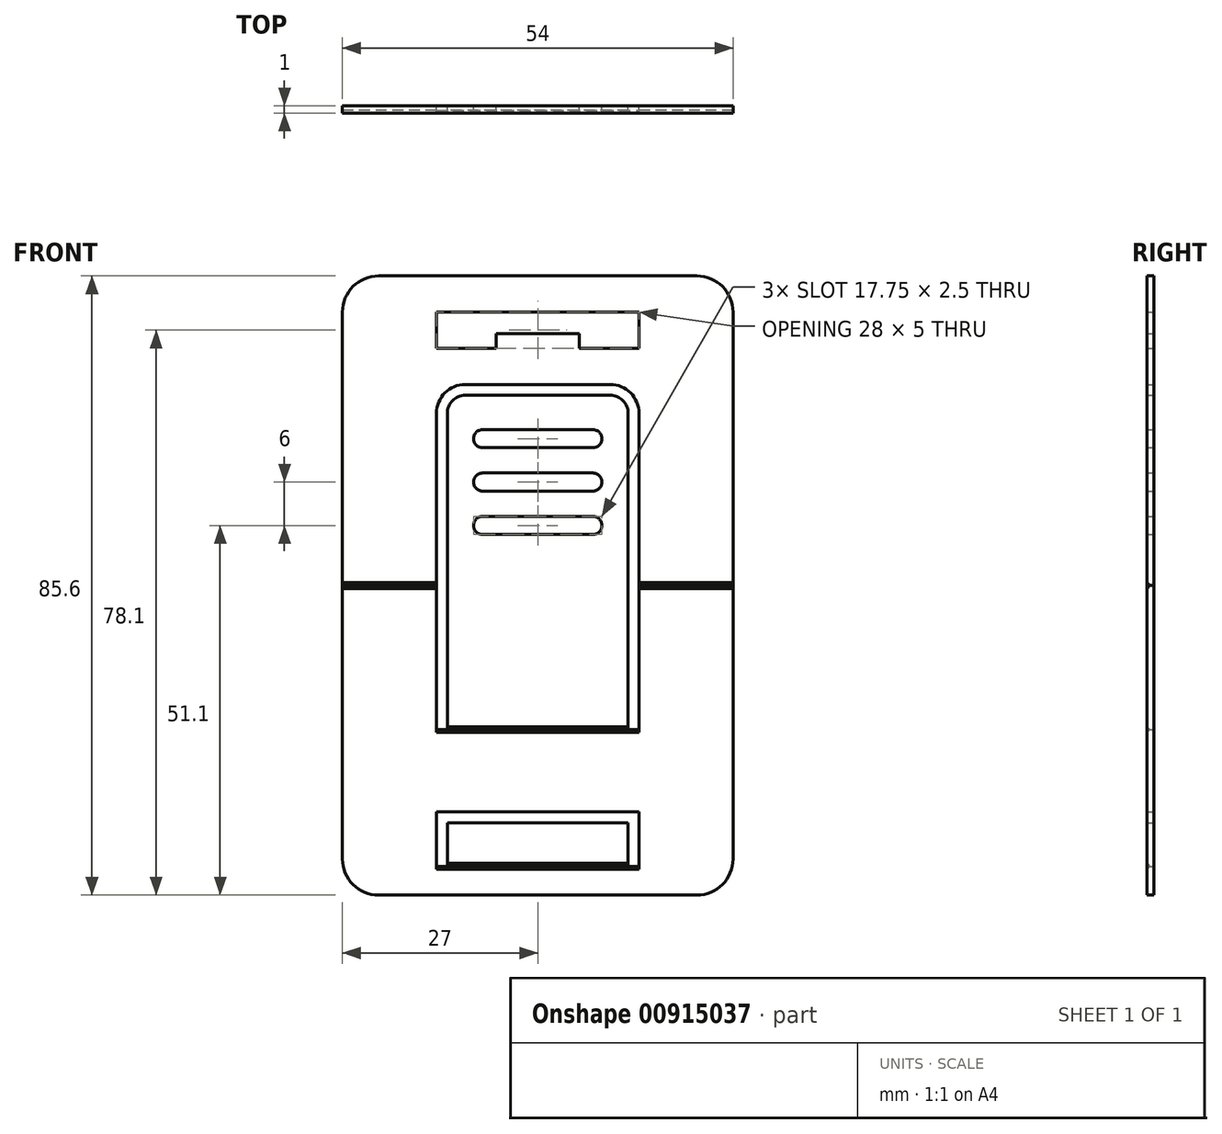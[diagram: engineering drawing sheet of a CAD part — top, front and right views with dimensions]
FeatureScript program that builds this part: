
annotation { "Feature Type Name" : "Feature", "Feature Type Description" : "" }
export const myFeature = defineFeature(function(context is Context, id is Id, definition is map)
    precondition{}
    {
        {
            var Q0;
            Q0=qCreatedBy(makeId("Front.planeOp"),FACE);
            var sketch = newSketch(context, id + "F0", { "sketchPlane" : qUnion([Q0])});
            skLineSegment(sketch, "E0.bottom", {"start": v(-22, 85.6) * mm, "end": v(22, 85.6) * mm});
            skLineSegment(sketch, "E0.top", {"start": v(-22, 0) * mm, "end": v(22, 0) * mm});
            skLineSegment(sketch, "E0.left", {"start": v(-27, 80.6) * mm, "end": v(-27, 5) * mm});
            skLineSegment(sketch, "E0.right", {"start": v(27, 80.6) * mm, "end": v(27, 5) * mm});
            skPoint(sketch, "E1.visualSharp", {"position": v(-27, 85.6) * mm});
            skArc(sketch, "E1.filletArc", {"start": v(-22, 85.6) * mm, "mid": v(-25.54, 84.14) * mm, "end": v(-27, 80.6) * mm});
            skPoint(sketch, "E2.visualSharp", {"position": v(-27, 0) * mm});
            skArc(sketch, "E2.filletArc", {"start": v(-27, 5) * mm, "mid": v(-25.54, 1.46) * mm, "end": v(-22, 0) * mm});
            skPoint(sketch, "E3.visualSharp", {"position": v(27, 0) * mm});
            skArc(sketch, "E3.filletArc", {"start": v(22, 0) * mm, "mid": v(25.54, 1.46) * mm, "end": v(27, 5) * mm});
            skPoint(sketch, "E4.visualSharp", {"position": v(27, 85.6) * mm});
            skArc(sketch, "E4.filletArc", {"start": v(27, 80.6) * mm, "mid": v(25.54, 84.14) * mm, "end": v(22, 85.6) * mm});
            skLineSegment(sketch, "E5.bottom", {"start": v(-10, 70.6) * mm, "end": v(10, 70.6) * mm});
            skLineSegment(sketch, "E5.left", {"start": v(-14, 66.6) * mm, "end": v(-14, 22.88) * mm});
            skLineSegment(sketch, "E5.right", {"start": v(14, 66.6) * mm, "end": v(14, 22.88) * mm});
            skPoint(sketch, "E6.visualSharp", {"position": v(-14, 70.6) * mm});
            skArc(sketch, "E6.filletArc", {"start": v(-10, 70.6) * mm, "mid": v(-12.83, 69.43) * mm, "end": v(-14, 66.6) * mm});
            skPoint(sketch, "E7.visualSharp", {"position": v(14, 70.6) * mm});
            skArc(sketch, "E7.filletArc", {"start": v(14, 66.6) * mm, "mid": v(12.83, 69.43) * mm, "end": v(10, 70.6) * mm});
            skPoint(sketch, "E8", {"position": v(0, 70.6) * mm});
            skPoint(sketch, "E9", {"position": v(0, 85.6) * mm});
            skLineSegment(sketch, "E10.0", {"start": v(-12.5, 66.6) * mm, "end": v(-12.5, 22.88) * mm});
            skLineSegment(sketch, "E10.1", {"start": v(12.5, 66.6) * mm, "end": v(12.5, 22.88) * mm});
            skArc(sketch, "E10.2", {"start": v(12.5, 66.6) * mm, "mid": v(11.77, 68.37) * mm, "end": v(10, 69.1) * mm});
            skLineSegment(sketch, "E10.3", {"start": v(-10, 69.1) * mm, "end": v(10, 69.1) * mm});
            skArc(sketch, "E10.4", {"start": v(-10, 69.1) * mm, "mid": v(-11.77, 68.37) * mm, "end": v(-12.5, 66.6) * mm});
            skLineSegment(sketch, "E11", {"start": v(-12.5, 22.88) * mm, "end": v(-14, 22.88) * mm});
            skLineSegment(sketch, "E12", {"start": v(12.5, 22.88) * mm, "end": v(14, 22.88) * mm});
            skLineSegment(sketch, "E13", {"start": v(-12.5, 22.88) * mm, "end": v(12.5, 22.88) * mm});
            skLineSegment(sketch, "E14.bottom", {"start": v(-14, 80.6) * mm, "end": v(14, 80.6) * mm});
            skLineSegment(sketch, "E14.top", {"start": v(-14, 75.6) * mm, "end": v(-5.74, 75.6) * mm});
            skLineSegment(sketch, "E14.left", {"start": v(-14, 80.6) * mm, "end": v(-14, 75.6) * mm});
            skLineSegment(sketch, "E14.right", {"start": v(14, 80.6) * mm, "end": v(14, 75.6) * mm});
            skPoint(sketch, "E15", {"position": v(0, 75.6) * mm});
            skLineSegment(sketch, "E16", {"start": v(-5.74, 75.6) * mm, "end": v(-5.74, 77.6) * mm});
            skLineSegment(sketch, "E17", {"start": v(-5.74, 77.6) * mm, "end": v(5.74, 77.6) * mm});
            skLineSegment(sketch, "E18", {"start": v(5.74, 77.6) * mm, "end": v(5.74, 75.6) * mm});
            skPoint(sketch, "E19", {"position": v(0, 77.6) * mm});
            skLineSegment(sketch, "E20.trimOffspring", {"start": v(5.74, 75.6) * mm, "end": v(14, 75.6) * mm});
            skLineSegment(sketch, "E21", {"start": v(-27, 42.8) * mm, "end": v(-14, 42.8) * mm});
            skLineSegment(sketch, "E22", {"start": v(27, 42.8) * mm, "end": v(14, 42.8) * mm});
            skLineSegment(sketch, "E23.top", {"start": v(-14, 11.5) * mm, "end": v(14, 11.5) * mm});
            skLineSegment(sketch, "E23.left", {"start": v(-14, 4) * mm, "end": v(-14, 11.5) * mm});
            skLineSegment(sketch, "E23.right", {"start": v(14, 4) * mm, "end": v(14, 11.5) * mm});
            skPoint(sketch, "E24", {"position": v(0, 11.5) * mm});
            skLineSegment(sketch, "E25.0", {"start": v(12.5, 4) * mm, "end": v(12.5, 10) * mm});
            skLineSegment(sketch, "E25.1", {"start": v(-12.5, 10) * mm, "end": v(12.5, 10) * mm});
            skLineSegment(sketch, "E25.2", {"start": v(-12.5, 4) * mm, "end": v(-12.5, 10) * mm});
            skLineSegment(sketch, "E26", {"start": v(-14, 4) * mm, "end": v(-12.5, 4) * mm});
            skLineSegment(sketch, "E27", {"start": v(12.5, 4) * mm, "end": v(14, 4) * mm});
            skLineSegment(sketch, "E28", {"start": v(-12.5, 4) * mm, "end": v(12.5, 4) * mm});
            skLineSegment(sketch, "E29", {"start": v(-7.62, 63.1) * mm, "end": v(7.62, 63.1) * mm, "construction": true});
            skLineSegment(sketch, "E30", {"start": v(-7.62, 57.1) * mm, "end": v(7.62, 57.1) * mm, "construction": true});
            skLineSegment(sketch, "E31", {"start": v(-7.62, 51.1) * mm, "end": v(7.62, 51.1) * mm, "construction": true});
            skLineSegment(sketch, "E32", {"start": v(0, 63.1) * mm, "end": v(0, 57.1) * mm, "construction": true});
            skLineSegment(sketch, "E33", {"start": v(0, 51.1) * mm, "end": v(0, 57.1) * mm, "construction": true});
            skArc(sketch, "E34.0.startCap", {"start": v(-7.62, 61.85) * mm, "mid": v(-8.87, 63.1) * mm, "end": v(-7.62, 64.35) * mm});
            skArc(sketch, "E34.0.endCap", {"start": v(7.62, 64.35) * mm, "mid": v(8.87, 63.1) * mm, "end": v(7.62, 61.85) * mm});
            skLineSegment(sketch, "E34.0.left", {"start": v(-7.62, 64.35) * mm, "end": v(7.62, 64.35) * mm});
            skLineSegment(sketch, "E34.0.right", {"start": v(-7.62, 61.85) * mm, "end": v(7.62, 61.85) * mm});
            skArc(sketch, "E34.1.startCap", {"start": v(-7.62, 55.85) * mm, "mid": v(-8.87, 57.1) * mm, "end": v(-7.62, 58.35) * mm});
            skArc(sketch, "E34.1.endCap", {"start": v(7.62, 58.35) * mm, "mid": v(8.87, 57.1) * mm, "end": v(7.62, 55.85) * mm});
            skLineSegment(sketch, "E34.1.left", {"start": v(-7.62, 58.35) * mm, "end": v(7.62, 58.35) * mm});
            skLineSegment(sketch, "E34.1.right", {"start": v(-7.62, 55.85) * mm, "end": v(7.62, 55.85) * mm});
            skArc(sketch, "E34.2.startCap", {"start": v(-7.62, 49.85) * mm, "mid": v(-8.87, 51.1) * mm, "end": v(-7.62, 52.35) * mm});
            skArc(sketch, "E34.2.endCap", {"start": v(7.62, 52.35) * mm, "mid": v(8.87, 51.1) * mm, "end": v(7.62, 49.85) * mm});
            skLineSegment(sketch, "E34.2.left", {"start": v(-7.62, 52.35) * mm, "end": v(7.62, 52.35) * mm});
            skLineSegment(sketch, "E34.2.right", {"start": v(-7.62, 49.85) * mm, "end": v(7.62, 49.85) * mm});
            skLineSegment(sketch, "E35", {"start": v(0, 63.1) * mm, "end": v(0, 69.1) * mm, "construction": true});
            skSolve(sketch);
        }
        {
            var Q0;
            {var subQ0=sQuery(id+"F0.wireOp",EDGE,"E10.2");Q0=makeQuery(id+"F0.imprint","IMPRINT",FACE,{"disambiguationData":[TD([[makeQuery(id+"F0.imprint","IMPRINT",EDGE,{"derivedFrom":subQ0}),1.0]])]});}
            extrude(context, id + "F1", {"entities" : qUnion([Q0]), "depth" : 1 * mm, "offsetDistance" : 25 * mm});
        }
        {
            var Q0;
            Q0=makeQuery(id+"F0.imprint","IMPRINT",FACE,{"disambiguationData":[TD([[makeQuery(id+"F0.imprint","IMPRINT",EDGE,{"derivedFrom":sQuery(id+"F0.wireOp",EDGE,"E0.bottom")}),-1.0]])]});
            extrude(context, id + "F2", {"entities" : qUnion([Q0]), "depth" : 1 * mm, "offsetDistance" : 25 * mm});
        }
        {
            var Q0;
            Q0=makeQuery(id+"F0.imprint","IMPRINT",FACE,{"disambiguationData":[TD([[makeQuery(id+"F0.imprint","IMPRINT",EDGE,{"derivedFrom":sQuery(id+"F0.wireOp",EDGE,"E0.top")}),1.0]])]});
            extrude(context, id + "F3", {"entities" : qUnion([Q0]), "depth" : 1 * mm, "offsetDistance" : 25 * mm});
        }
        {
            var Q0;
            Q0=makeQuery(id+"F0.imprint","IMPRINT",FACE,{"disambiguationData":[TD([[makeQuery(id+"F0.imprint","IMPRINT",EDGE,{"derivedFrom":sQuery(id+"F0.wireOp",EDGE,"E25.0")}),1.0]])]});
            extrude(context, id + "F4", {"entities" : qUnion([Q0]), "depth" : 1 * mm, "offsetDistance" : 25 * mm});
        }
        {
            var Q0;
            Q0=makeQuery(id+"F1.opExtrude","CAP_EDGE",EDGE,{"disambiguationData":[OSD([sQuery(id+"F0.wireOp",EDGE,"E13")])],"isStart":false});
            var Q1;
            Q1=makeQuery(id+"F2.opExtrude","CAP_EDGE",EDGE,{"disambiguationData":[OSD([sQuery(id+"F0.wireOp",EDGE,"E21")])],"isStart":false});
            var Q2;
            Q2=makeQuery(id+"F2.opExtrude","CAP_EDGE",EDGE,{"disambiguationData":[OSD([sQuery(id+"F0.wireOp",EDGE,"E22")])],"isStart":false});
            var Q3;
            Q3=makeQuery(id+"F3.opExtrude","CAP_EDGE",EDGE,{"disambiguationData":[OSD([sQuery(id+"F0.wireOp",EDGE,"E21")])],"isStart":false});
            var Q4;
            Q4=makeQuery(id+"F3.opExtrude","CAP_EDGE",EDGE,{"disambiguationData":[OSD([sQuery(id+"F0.wireOp",EDGE,"E22")])],"isStart":false});
            var Q5;
            Q5=makeQuery(id+"F3.opExtrude","CAP_EDGE",EDGE,{"disambiguationData":[OSD([sQuery(id+"F0.wireOp",EDGE,"E26"),sQuery(id+"F0.wireOp",EDGE,"E27"),sQuery(id+"F0.wireOp",EDGE,"E28")])],"isStart":false});
            var Q6;
            Q6=makeQuery(id+"F4.opExtrude","CAP_EDGE",EDGE,{"disambiguationData":[OSD([sQuery(id+"F0.wireOp",EDGE,"E28")])],"isStart":false});
            var Q7;
            Q7=makeQuery(id+"F3.opExtrude","CAP_EDGE",EDGE,{"disambiguationData":[OSD([sQuery(id+"F0.wireOp",EDGE,"E11"),sQuery(id+"F0.wireOp",EDGE,"E12"),sQuery(id+"F0.wireOp",EDGE,"E13")])],"isStart":false});
            chamfer(context, id + "F5", {"entities" : qUnion([Q0, Q1, Q2, Q3, Q4, Q5, Q6, Q7]), "width" : .4 * mm, "tangentPropagation" : true});
        }
    });
